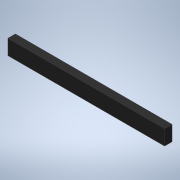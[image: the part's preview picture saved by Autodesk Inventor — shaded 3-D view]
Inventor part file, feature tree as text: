
AUTODESK INVENTOR PART (.ipt)
format: ipt  version: 2020 (Build 240168000, 168)  size: 97,792 bytes
history: native  units: mm
features: other x1, extrude x1
ambient origin geometry x8: Origin, YZ Plane, XZ Plane, XY Plane, X Axis, Y Axis, Z Axis, Center Point
bodies: Body1 (feature_tree)
feature tree (2):
  other  "實體1"
  extrude  "擠出1"  Depth=12.0mm
